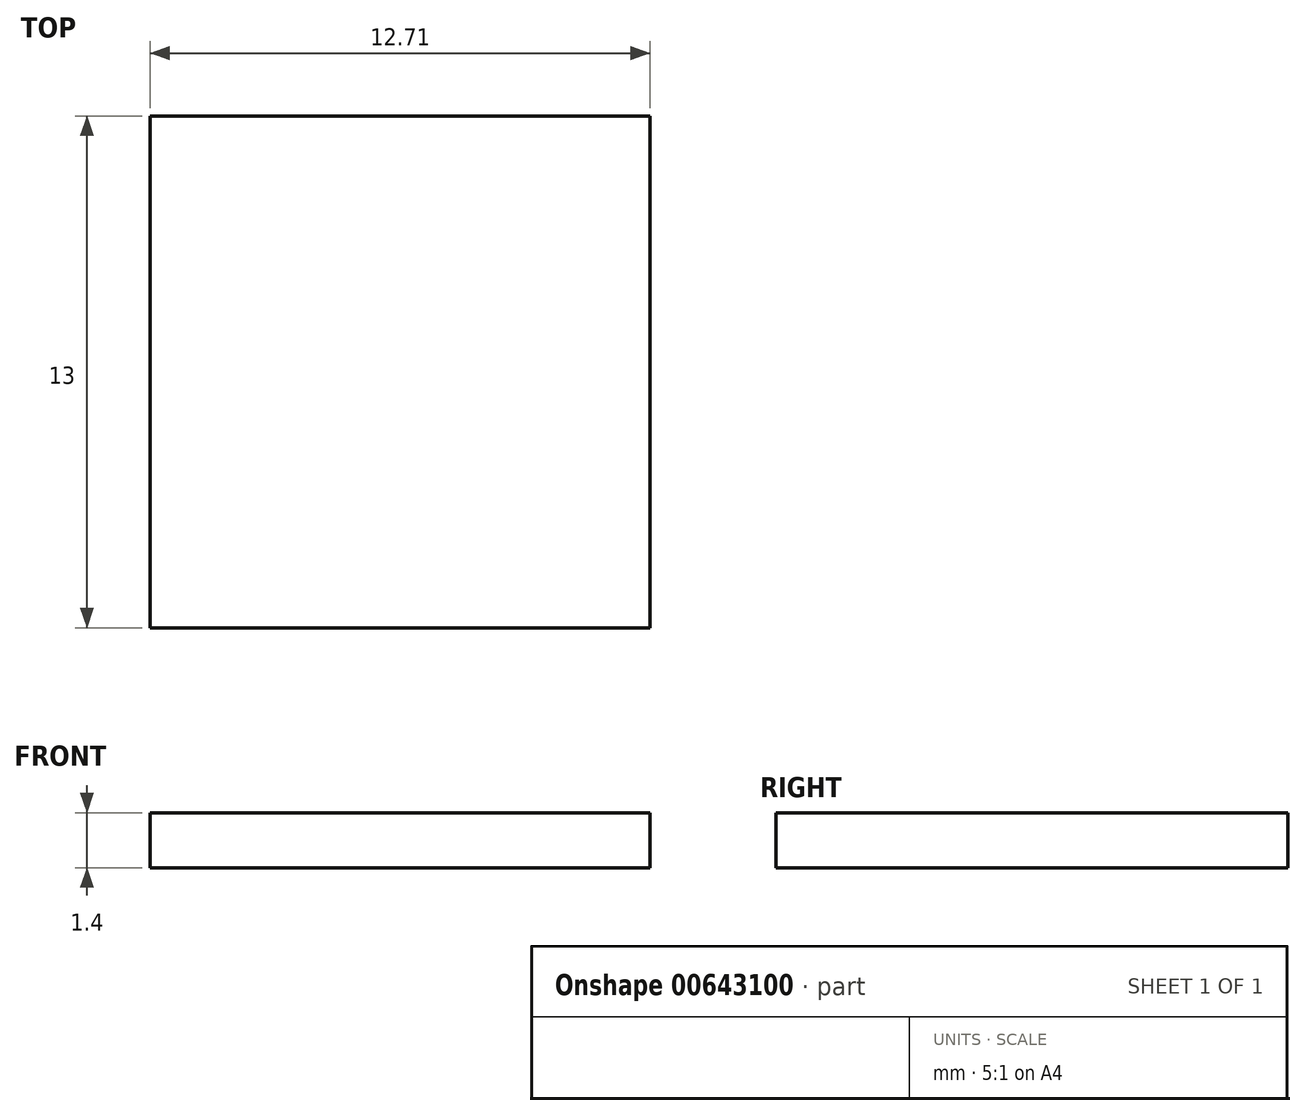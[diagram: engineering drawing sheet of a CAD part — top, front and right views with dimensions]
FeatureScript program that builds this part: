
annotation { "Feature Type Name" : "Feature", "Feature Type Description" : "" }
export const myFeature = defineFeature(function(context is Context, id is Id, definition is map)
    precondition{}
    {
        {
            var Q0;
            Q0=qCreatedBy(makeId("Top.planeOp"),FACE);
            var sketch = newSketch(context, id + "F0", { "sketchPlane" : qUnion([Q0])});
            skLineSegment(sketch, "E0.bottom", {"start": v(-29.04, 18.75) * mm, "end": v(-16.33, 18.75) * mm});
            skLineSegment(sketch, "E0.top", {"start": v(-29.04, 5.75) * mm, "end": v(-16.33, 5.75) * mm});
            skLineSegment(sketch, "E0.left", {"start": v(-29.04, 18.75) * mm, "end": v(-29.04, 5.75) * mm});
            skLineSegment(sketch, "E0.right", {"start": v(-16.33, 18.75) * mm, "end": v(-16.33, 5.75) * mm});
            skSolve(sketch);
        }
        {
            var Q0;
            Q0=makeQuery(id+"F0.imprint","IMPRINT",FACE,{"disambiguationData":[TD([[makeQuery(id+"F0.imprint","IMPRINT",EDGE,{"derivedFrom":sQuery(id+"F0.wireOp",EDGE,"E0.bottom")}),-1.0]])]});
            extrude(context, id + "F1", {"entities" : qUnion([Q0]), "depth" : 1.4 * mm, "offsetDistance" : 25.4 * mm});
        }
        {
            var Q0;
            Q0=makeQuery(id+"F1.opExtrude","SWEPT_BODY",BODY,{"disambiguationData":[OSD([sQuery(id+"F0.wireOp",EDGE,"E0.bottom"),sQuery(id+"F0.wireOp",EDGE,"E0.top"),sQuery(id+"F0.wireOp",EDGE,"E0.left"),sQuery(id+"F0.wireOp",EDGE,"E0.right")])]});
            var Q1;
            Q1=makeQuery(id+"F1.opExtrude","CAP_FACE",FACE,{"disambiguationData":[OSD([sQuery(id+"F0.wireOp",EDGE,"E0.bottom"),sQuery(id+"F0.wireOp",EDGE,"E0.top"),sQuery(id+"F0.wireOp",EDGE,"E0.left"),sQuery(id+"F0.wireOp",EDGE,"E0.right")])],"isStart":false});
            transform(context, id + "F2", {"entities" : qUnion([Q0]), "transformType" : TransformType.TRANSLATION_DISTANCE, "transformDirection" : qUnion([Q1]), "distance" : 25.4 * mm, "makeCopy" : false});
        }
    });
